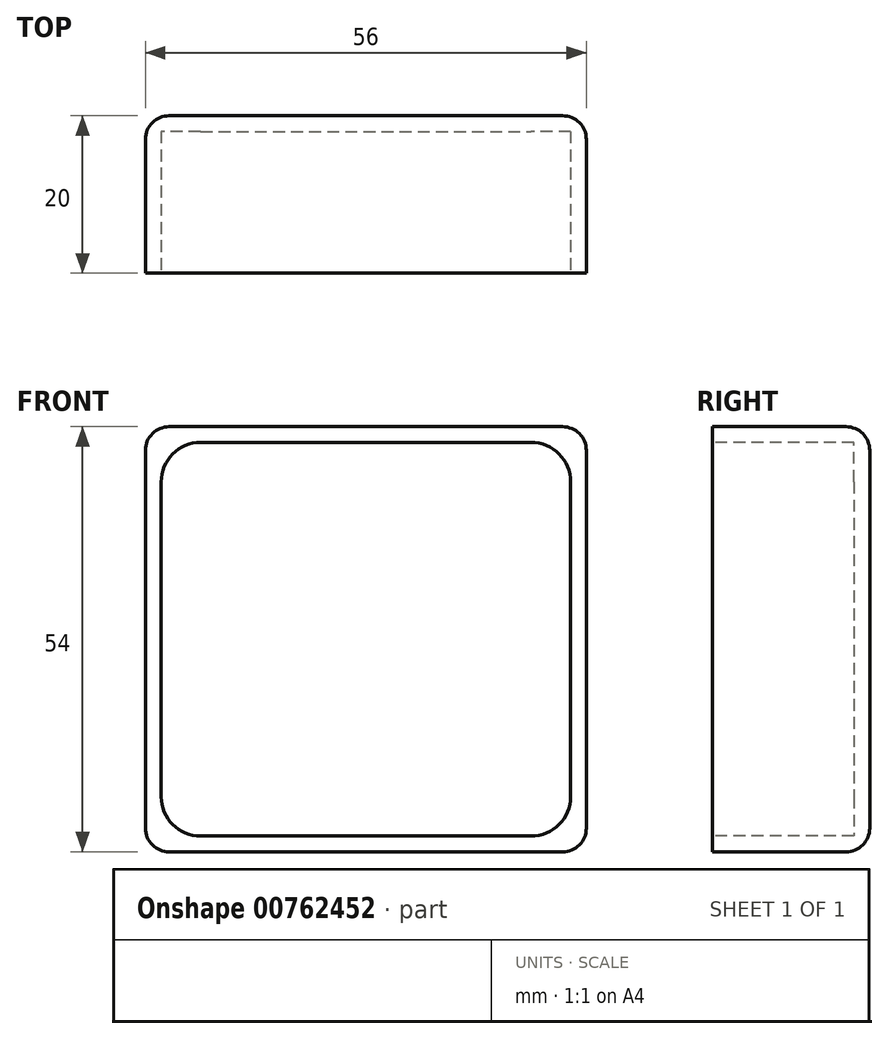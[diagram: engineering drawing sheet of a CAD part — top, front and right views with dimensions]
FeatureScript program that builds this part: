
annotation { "Feature Type Name" : "Feature", "Feature Type Description" : "" }
export const myFeature = defineFeature(function(context is Context, id is Id, definition is map)
    precondition{}
    {
        {
            var Q0;
            Q0=qCreatedBy(makeId("Front.planeOp"),FACE);
            var sketch = newSketch(context, id + "F0", { "sketchPlane" : qUnion([Q0])});
            skLineSegment(sketch, "E0.bottom", {"start": v(-19.8, 23.13) * mm, "end": v(36.2, 23.13) * mm});
            skLineSegment(sketch, "E0.top", {"start": v(-19.8, -30.87) * mm, "end": v(36.2, -30.87) * mm});
            skLineSegment(sketch, "E0.left", {"start": v(-19.8, 23.13) * mm, "end": v(-19.8, -30.87) * mm});
            skLineSegment(sketch, "E0.right", {"start": v(36.2, 23.13) * mm, "end": v(36.2, -30.87) * mm});
            skSolve(sketch);
        }
        {
            var Q0;
            Q0=makeQuery(id+"F0.imprint","IMPRINT",FACE,{"disambiguationData":[TD([[makeQuery(id+"F0.imprint","IMPRINT",EDGE,{"derivedFrom":sQuery(id+"F0.wireOp",EDGE,"E0.bottom")}),-1.0]])]});
            extrude(context, id + "F1", {"entities" : qUnion([Q0]), "depth" : 20 * mm, "offsetDistance" : 25 * mm});
        }
        {
            var Q0;
            Q0=makeQuery(id+"F1.opExtrude","CAP_FACE",FACE,{"disambiguationData":[OSD([sQuery(id+"F0.wireOp",EDGE,"E0.bottom"),sQuery(id+"F0.wireOp",EDGE,"E0.top"),sQuery(id+"F0.wireOp",EDGE,"E0.left"),sQuery(id+"F0.wireOp",EDGE,"E0.right")])],"isStart":false});
            var sketch = newSketch(context, id + "F2", { "sketchPlane" : qUnion([Q0])});
            skLineSegment(sketch, "E1.bottom", {"start": v(-12.8, 21.13) * mm, "end": v(29.2, 21.13) * mm});
            skLineSegment(sketch, "E1.top", {"start": v(-12.8, -28.87) * mm, "end": v(29.2, -28.87) * mm});
            skLineSegment(sketch, "E1.left", {"start": v(-17.8, 16.13) * mm, "end": v(-17.8, -23.87) * mm});
            skLineSegment(sketch, "E1.right", {"start": v(34.2, 16.13) * mm, "end": v(34.2, -23.87) * mm});
            skPoint(sketch, "E2.visualSharp", {"position": v(-17.8, 21.13) * mm});
            skArc(sketch, "E2.filletArc", {"start": v(-12.8, 21.13) * mm, "mid": v(-16.33, 19.66) * mm, "end": v(-17.8, 16.13) * mm});
            skPoint(sketch, "E3.visualSharp", {"position": v(34.2, 21.13) * mm});
            skArc(sketch, "E3.filletArc", {"start": v(34.2, 16.13) * mm, "mid": v(32.74, 19.66) * mm, "end": v(29.2, 21.13) * mm});
            skPoint(sketch, "E4.visualSharp", {"position": v(34.2, -28.87) * mm});
            skArc(sketch, "E4.filletArc", {"start": v(29.2, -28.87) * mm, "mid": v(32.74, -27.4) * mm, "end": v(34.2, -23.87) * mm});
            skPoint(sketch, "E5.visualSharp", {"position": v(-17.8, -28.87) * mm});
            skArc(sketch, "E5.filletArc", {"start": v(-17.8, -23.87) * mm, "mid": v(-16.33, -27.4) * mm, "end": v(-12.8, -28.87) * mm});
            skSolve(sketch);
        }
        {
            var Q0;
            Q0 = qSketchRegion(id + "F2", true);
            extrude(context, id + "F3", {"entities" : qUnion([Q0]), "operationType" : NewBodyOperationType.REMOVE, "oppositeDirection" : true, "depth" : 18 * mm, "offsetDistance" : 25 * mm});
        }
        {
            var Q0;
            Q0=makeQuery(id+"F1.opExtrude","SWEPT_EDGE",EDGE,{"disambiguationData":[OSD([sQuery(id+"F0.wireOp",EDGE,"E0.bottom"),sQuery(id+"F0.wireOp",EDGE,"E0.right")])]});
            var Q1;
            Q1=makeQuery(id+"F1.opExtrude","SWEPT_EDGE",EDGE,{"disambiguationData":[OSD([sQuery(id+"F0.wireOp",EDGE,"E0.bottom"),sQuery(id+"F0.wireOp",EDGE,"E0.left")])]});
            var Q2;
            Q2=makeQuery(id+"F1.opExtrude","SWEPT_EDGE",EDGE,{"disambiguationData":[OSD([sQuery(id+"F0.wireOp",EDGE,"E0.top"),sQuery(id+"F0.wireOp",EDGE,"E0.right")])]});
            var Q3;
            Q3=makeQuery(id+"F1.opExtrude","SWEPT_EDGE",EDGE,{"disambiguationData":[OSD([sQuery(id+"F0.wireOp",EDGE,"E0.top"),sQuery(id+"F0.wireOp",EDGE,"E0.left")])]});
            fillet(context, id + "F4", {"entities" : qUnion([Q0, Q1, Q2, Q3]), "radius" : 3 * mm, "tangentPropagation" : true, "allowEdgeOverflow" : false});
        }
        {
            var Q0;
            Q0=makeQuery(id+"F1.opExtrude","CAP_EDGE",EDGE,{"disambiguationData":[OSD([sQuery(id+"F0.wireOp",EDGE,"E0.bottom")])],"isStart":true});
            fillet(context, id + "F5", {"entities" : qUnion([Q0]), "radius" : 3 * mm, "tangentPropagation" : true, "allowEdgeOverflow" : false});
        }
    });
